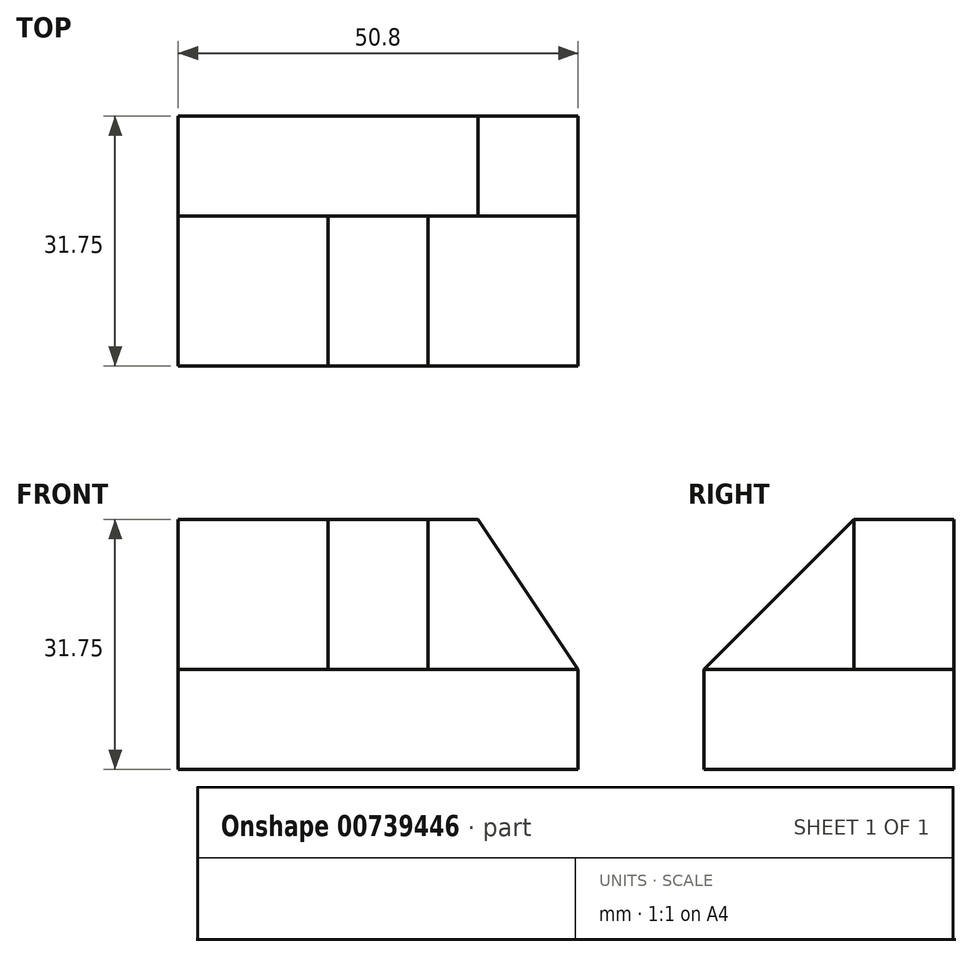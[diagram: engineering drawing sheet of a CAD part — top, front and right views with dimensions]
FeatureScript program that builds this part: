
annotation { "Feature Type Name" : "Feature", "Feature Type Description" : "" }
export const myFeature = defineFeature(function(context is Context, id is Id, definition is map)
    precondition{}
    {
        {
            var Q0;
            Q0=qCreatedBy(makeId("Front.planeOp"),FACE);
            var sketch = newSketch(context, id + "F0", { "sketchPlane" : qUnion([Q0])});
            skLineSegment(sketch, "E0.bottom", {"start": v(0, 0) * mm, "end": v(50.8, 0) * mm});
            skLineSegment(sketch, "E0.top", {"start": v(0, 31.75) * mm, "end": v(50.8, 31.75) * mm});
            skLineSegment(sketch, "E0.left", {"start": v(0, 0) * mm, "end": v(0, 31.75) * mm});
            skLineSegment(sketch, "E0.right", {"start": v(50.8, 0) * mm, "end": v(50.8, 31.75) * mm});
            skSolve(sketch);
        }
        {
            var Q0;
            Q0=makeQuery(id+"F0.imprint","IMPRINT",FACE,{"disambiguationData":[TD([[makeQuery(id+"F0.imprint","IMPRINT",EDGE,{"derivedFrom":sQuery(id+"F0.wireOp",EDGE,"E0.bottom")}),1.0]])]});
            extrude(context, id + "F1", {"entities" : qUnion([Q0]), "depth" : 31.75 * mm, "offsetDistance" : 25.4 * mm});
        }
        {
            var Q0;
            Q0=makeQuery(id+"F1.opExtrude","CAP_FACE",FACE,{"disambiguationData":[OSD([sQuery(id+"F0.wireOp",EDGE,"E0.bottom"),sQuery(id+"F0.wireOp",EDGE,"E0.top"),sQuery(id+"F0.wireOp",EDGE,"E0.left"),sQuery(id+"F0.wireOp",EDGE,"E0.right")])],"isStart":false});
            var sketch = newSketch(context, id + "F2", { "sketchPlane" : qUnion([Q0])});
            skLineSegment(sketch, "E1.bottom", {"start": v(0, 31.75) * mm, "end": v(19.05, 31.75) * mm});
            skLineSegment(sketch, "E1.top", {"start": v(0, 12.7) * mm, "end": v(19.05, 12.7) * mm});
            skLineSegment(sketch, "E1.left", {"start": v(0, 31.75) * mm, "end": v(0, 12.7) * mm});
            skLineSegment(sketch, "E1.right", {"start": v(19.05, 31.75) * mm, "end": v(19.05, 12.7) * mm});
            skLineSegment(sketch, "E2.bottom", {"start": v(50.8, 31.75) * mm, "end": v(31.75, 31.75) * mm});
            skLineSegment(sketch, "E2.top", {"start": v(50.8, 12.7) * mm, "end": v(31.75, 12.7) * mm});
            skLineSegment(sketch, "E2.left", {"start": v(50.8, 31.75) * mm, "end": v(50.8, 12.7) * mm});
            skLineSegment(sketch, "E2.right", {"start": v(31.75, 31.75) * mm, "end": v(31.75, 12.7) * mm});
            skSolve(sketch);
        }
        {
            var Q0;
            Q0=makeQuery(id+"F2.imprint","IMPRINT",FACE,{"disambiguationData":[TD([[makeQuery(id+"F2.imprint","IMPRINT",EDGE,{"derivedFrom":sQuery(id+"F2.wireOp",EDGE,"E1.bottom")}),-1.0]])]});
            var Q1;
            Q1=makeQuery(id+"F2.imprint","IMPRINT",FACE,{"disambiguationData":[TD([[makeQuery(id+"F2.imprint","IMPRINT",EDGE,{"derivedFrom":sQuery(id+"F2.wireOp",EDGE,"E2.bottom")}),-1.0]])]});
            extrude(context, id + "F3", {"entities" : qUnion([Q0, Q1]), "operationType" : NewBodyOperationType.REMOVE, "oppositeDirection" : true, "depth" : 19.05 * mm, "offsetDistance" : 25.4 * mm});
        }
        {
            var Q0;
            Q0=makeQuery(id+"F3.boolean.opBoolean","COPY",FACE,{"derivedFrom":makeQuery(id+"F3.opExtrude","SWEPT_FACE",FACE,{"disambiguationData":[OSD([sQuery(id+"F2.wireOp",EDGE,"E2.right")])]})});
            var sketch = newSketch(context, id + "F4", { "sketchPlane" : qUnion([Q0])});
            skLineSegment(sketch, "E3", {"start": v(-12.7, 31.75) * mm, "end": v(-31.75, 12.7) * mm});
            skLineSegment(sketch, "E4", {"start": v(-31.75, 12.7) * mm, "end": v(-31.75, 31.75) * mm});
            skLineSegment(sketch, "E5", {"start": v(-31.75, 31.75) * mm, "end": v(-12.7, 31.75) * mm});
            skSolve(sketch);
        }
        {
            var Q0;
            Q0=makeQuery(id+"F4.imprint","IMPRINT",FACE,{"disambiguationData":[TD([[makeQuery(id+"F4.imprint","IMPRINT",EDGE,{"derivedFrom":sQuery(id+"F4.wireOp",EDGE,"E3")}),-1.0]])]});
            extrude(context, id + "F5", {"entities" : qUnion([Q0]), "operationType" : NewBodyOperationType.REMOVE, "oppositeDirection" : true, "depth" : 12.7 * mm, "offsetDistance" : 25.4 * mm});
        }
        {
            var Q0;
            Q0=makeQuery(id+"F3.boolean.opBoolean","COPY",FACE,{"derivedFrom":makeQuery(id+"F3.opExtrude","CAP_FACE",FACE,{"disambiguationData":[OSD([sQuery(id+"F2.wireOp",EDGE,"E2.bottom"),sQuery(id+"F2.wireOp",EDGE,"E2.top"),sQuery(id+"F2.wireOp",EDGE,"E2.left"),sQuery(id+"F2.wireOp",EDGE,"E2.right")])],"isStart":false})});
            var sketch = newSketch(context, id + "F6", { "sketchPlane" : qUnion([Q0])});
            skLineSegment(sketch, "E6", {"start": v(38.1, 31.75) * mm, "end": v(50.8, 12.7) * mm});
            skLineSegment(sketch, "E7", {"start": v(50.8, 12.7) * mm, "end": v(50.8, 31.75) * mm});
            skLineSegment(sketch, "E8", {"start": v(50.8, 31.75) * mm, "end": v(38.1, 31.75) * mm});
            skSolve(sketch);
        }
        {
            var Q0;
            Q0=makeQuery(id+"F6.imprint","IMPRINT",FACE,{"disambiguationData":[TD([[makeQuery(id+"F6.imprint","IMPRINT",EDGE,{"derivedFrom":sQuery(id+"F6.wireOp",EDGE,"E6")}),1.0]])]});
            extrude(context, id + "F7", {"entities" : qUnion([Q0]), "operationType" : NewBodyOperationType.REMOVE, "oppositeDirection" : true, "depth" : 12.7 * mm, "offsetDistance" : 25.4 * mm});
        }
    });
